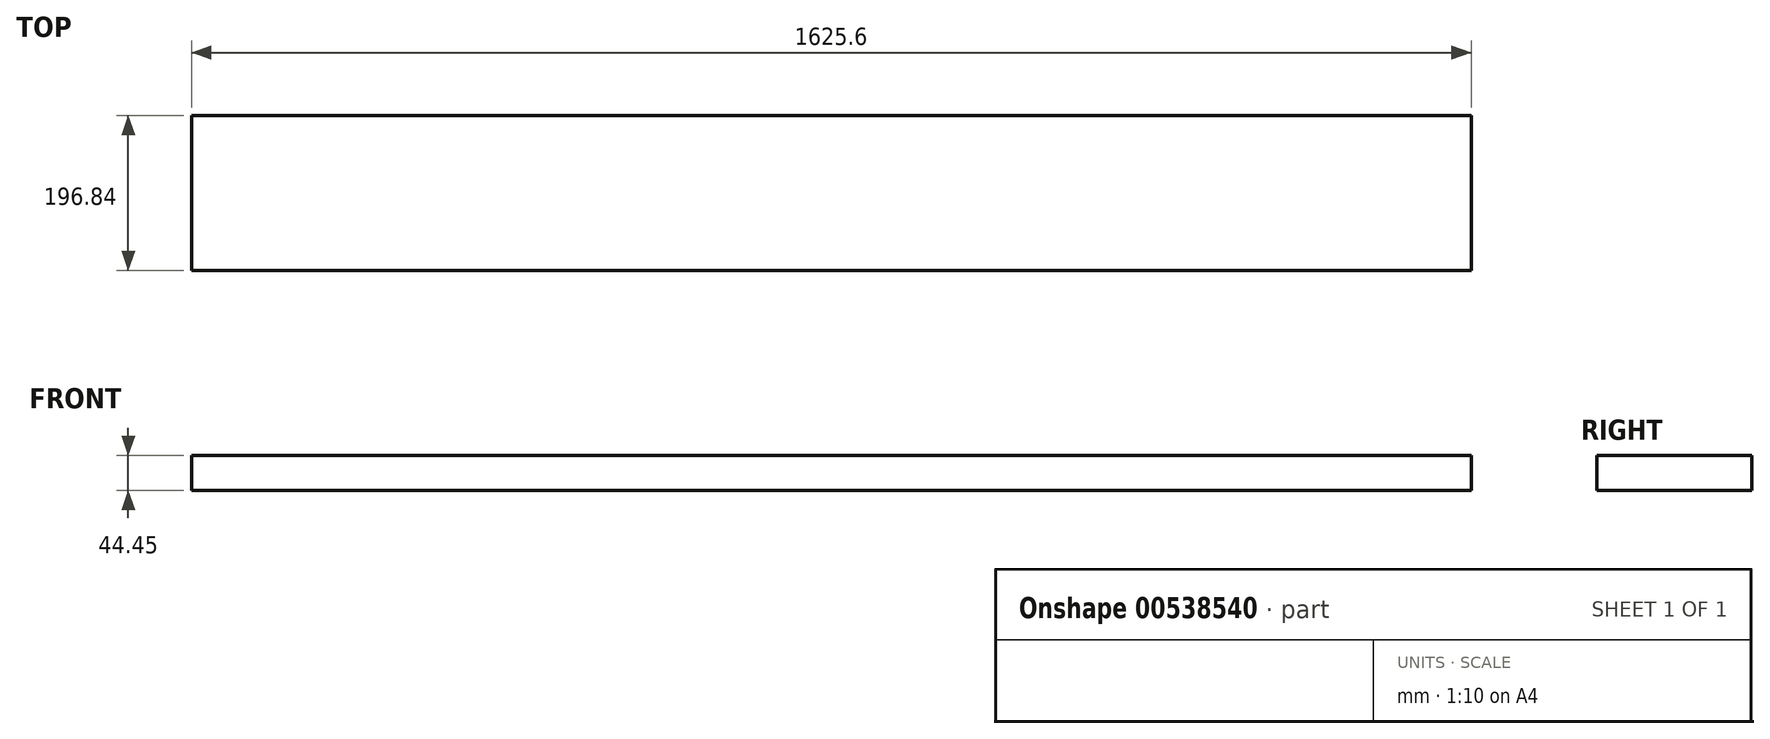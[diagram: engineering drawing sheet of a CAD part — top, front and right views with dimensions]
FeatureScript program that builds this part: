
annotation { "Feature Type Name" : "Feature", "Feature Type Description" : "" }
export const myFeature = defineFeature(function(context is Context, id is Id, definition is map)
    precondition{}
    {
        {
            var Q0;
            Q0=qCreatedBy(makeId("Top.planeOp"),FACE);
            var sketch = newSketch(context, id + "F0", { "sketchPlane" : qUnion([Q0])});
            skLineSegment(sketch, "E0.bottom", {"start": v(-812.8, 98.43) * mm, "end": v(812.8, 98.43) * mm});
            skLineSegment(sketch, "E0.top", {"start": v(-812.8, -98.42) * mm, "end": v(812.8, -98.42) * mm});
            skLineSegment(sketch, "E0.left", {"start": v(-812.8, 98.43) * mm, "end": v(-812.8, -98.42) * mm});
            skLineSegment(sketch, "E0.right", {"start": v(812.8, 98.43) * mm, "end": v(812.8, -98.42) * mm});
            skPoint(sketch, "E0.middle", {"position": v(0, 0) * mm});
            skSolve(sketch);
        }
        {
            var Q0;
            Q0 = qSketchRegion(id + "F0", true);
            extrude(context, id + "F1", {"entities" : qUnion([Q0]), "depth" : 44.45 * mm, "offsetDistance" : 25.4 * mm});
        }
    });
